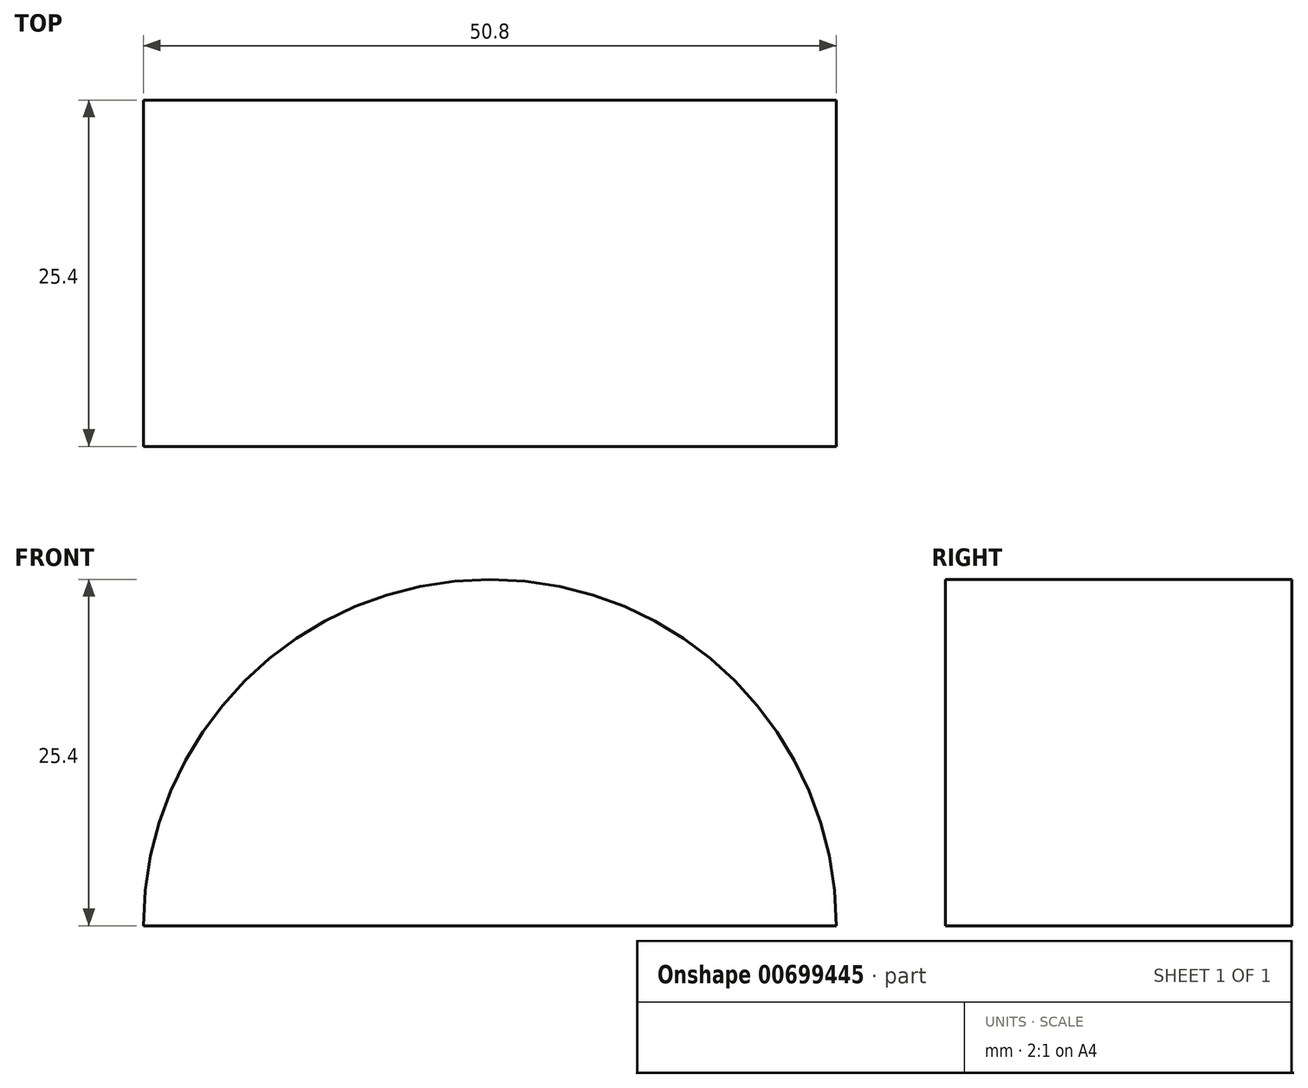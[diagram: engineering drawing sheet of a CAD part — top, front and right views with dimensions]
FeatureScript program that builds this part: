
annotation { "Feature Type Name" : "Feature", "Feature Type Description" : "" }
export const myFeature = defineFeature(function(context is Context, id is Id, definition is map)
    precondition{}
    {
        {
            var Q0;
            Q0=qCreatedBy(makeId("Front.planeOp"),FACE);
            var sketch = newSketch(context, id + "F0", { "sketchPlane" : qUnion([Q0])});
            skLineSegment(sketch, "E0.bottom", {"start": v(469.9, 431.8) * mm, "end": v(-469.9, 431.8) * mm});
            skLineSegment(sketch, "E0.top", {"start": v(469.9, -431.8) * mm, "end": v(-469.9, -431.8) * mm});
            skLineSegment(sketch, "E0.left", {"start": v(469.9, 431.8) * mm, "end": v(469.9, -431.8) * mm});
            skLineSegment(sketch, "E0.right", {"start": v(-469.9, 431.8) * mm, "end": v(-469.9, -431.8) * mm});
            skPoint(sketch, "E0.middle", {"position": v(0, 0) * mm});
            skLineSegment(sketch, "E1.bottom", {"start": v(355.6, 431.8) * mm, "end": v(330.2, 431.8) * mm});
            skLineSegment(sketch, "E1.top", {"start": v(355.6, 279.4) * mm, "end": v(330.2, 279.4) * mm});
            skLineSegment(sketch, "E1.left", {"start": v(355.6, 431.8) * mm, "end": v(355.6, 279.4) * mm});
            skLineSegment(sketch, "E1.right", {"start": v(330.2, 431.8) * mm, "end": v(330.2, 279.4) * mm});
            skLineSegment(sketch, "E2.bottom", {"start": v(-228.6, 431.8) * mm, "end": v(-254, 431.8) * mm});
            skLineSegment(sketch, "E2.top", {"start": v(-228.6, 279.4) * mm, "end": v(-254, 279.4) * mm});
            skLineSegment(sketch, "E2.left", {"start": v(-228.6, 431.8) * mm, "end": v(-228.6, 279.4) * mm});
            skLineSegment(sketch, "E2.right", {"start": v(-254, 431.8) * mm, "end": v(-254, 279.4) * mm});
            skLineSegment(sketch, "E3.bottom", {"start": v(469.9, 431.8) * mm, "end": v(444.5, 431.8) * mm});
            skLineSegment(sketch, "E3.top", {"start": v(469.9, 457.2) * mm, "end": v(444.5, 457.2) * mm});
            skLineSegment(sketch, "E3.left", {"start": v(469.9, 431.8) * mm, "end": v(469.9, 457.2) * mm});
            skLineSegment(sketch, "E3.right", {"start": v(444.5, 431.8) * mm, "end": v(444.5, 457.2) * mm});
            skArc(sketch, "E4", {"start": v(469.9, 457.2) * mm, "mid": v(444.5, 482.6) * mm, "end": v(419.1, 457.2) * mm});
            skLineSegment(sketch, "E5", {"start": v(444.5, 457.2) * mm, "end": v(419.1, 457.2) * mm});
            skSolve(sketch);
        }
        {
            var Q0;
            Q0=makeQuery(id+"F0.imprint","IMPRINT",FACE,{"disambiguationData":[TD([[makeQuery(id+"F0.imprint","IMPRINT",EDGE,{"derivedFrom":sQuery(id+"F0.wireOp",EDGE,"E3.top")}),-1.0]])]});
            var Q1;
            Q1=makeQuery(id+"F0.imprint","IMPRINT",FACE,{"disambiguationData":[TD([[makeQuery(id+"F0.imprint","IMPRINT",EDGE,{"derivedFrom":sQuery(id+"F0.wireOp",EDGE,"E3.bottom")}),-1.0]])]});
            var Q2;
            Q2=makeQuery(id+"F0.imprint","IMPRINT",FACE,{"disambiguationData":[TD([[makeQuery(id+"F0.imprint","IMPRINT",EDGE,{"derivedFrom":sQuery(id+"F0.wireOp",EDGE,"E0.top")}),-1.0]])]});
            extrude(context, id + "F1", {"entities" : qUnion([Q0, Q1, Q2]), "depth" : 25.4 * mm, "offsetDistance" : 25.4 * mm, "symmetric" : true});
        }
    });
